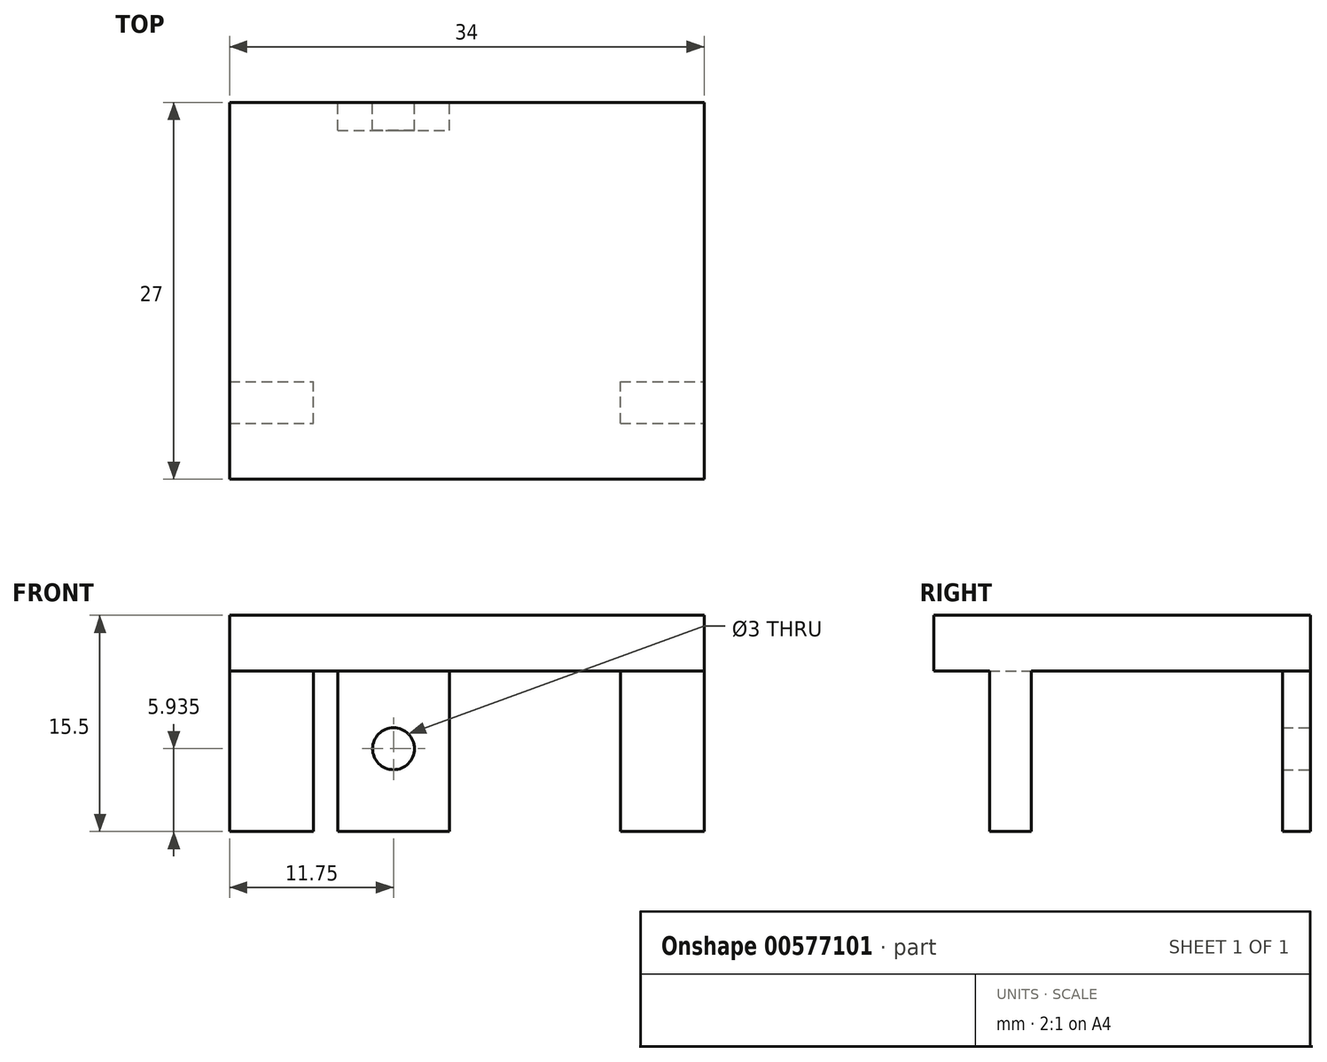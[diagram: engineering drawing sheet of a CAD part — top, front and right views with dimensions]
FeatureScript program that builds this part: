
annotation { "Feature Type Name" : "Feature", "Feature Type Description" : "" }
export const myFeature = defineFeature(function(context is Context, id is Id, definition is map)
    precondition{}
    {
        {
            var Q0;
            Q0=qCreatedBy(makeId("Front.planeOp"),FACE);
            var sketch = newSketch(context, id + "F0", { "sketchPlane" : qUnion([Q0])});
            skLineSegment(sketch, "E0.bottom", {"start": v(0, 0) * mm, "end": v(6, 0) * mm});
            skLineSegment(sketch, "E0.top", {"start": v(0, 15.5) * mm, "end": v(34, 15.5) * mm});
            skLineSegment(sketch, "E0.left", {"start": v(0, 0) * mm, "end": v(0, 15.5) * mm});
            skLineSegment(sketch, "E0.right", {"start": v(34, 0) * mm, "end": v(34, 15.5) * mm});
            skLineSegment(sketch, "E1.top", {"start": v(6, 11.5) * mm, "end": v(28, 11.5) * mm});
            skLineSegment(sketch, "E1.left", {"start": v(6, 0) * mm, "end": v(6, 11.5) * mm});
            skLineSegment(sketch, "E1.right", {"start": v(28, 0) * mm, "end": v(28, 11.5) * mm});
            skLineSegment(sketch, "E2.trimOffspring", {"start": v(28, 0) * mm, "end": v(34, 0) * mm});
            skSolve(sketch);
        }
        {
            var Q0;
            Q0=makeQuery(id+"F0.imprint","IMPRINT",FACE,{"disambiguationData":[TD([[makeQuery(id+"F0.imprint","IMPRINT",EDGE,{"derivedFrom":sQuery(id+"F0.wireOp",EDGE,"E0.bottom")}),1.0]])]});
            extrude(context, id + "F1", {"entities" : qUnion([Q0]), "depth" : 3 * mm, "offsetDistance" : 25 * mm});
        }
        {
            var Q0;
            Q0=makeQuery(id+"F1.opExtrude","CAP_FACE",FACE,{"disambiguationData":[OSD([sQuery(id+"F0.wireOp",EDGE,"E0.bottom"),sQuery(id+"F0.wireOp",EDGE,"E0.top"),sQuery(id+"F0.wireOp",EDGE,"E0.left"),sQuery(id+"F0.wireOp",EDGE,"E0.right"),sQuery(id+"F0.wireOp",EDGE,"E1.top"),sQuery(id+"F0.wireOp",EDGE,"E1.left"),sQuery(id+"F0.wireOp",EDGE,"E1.right"),sQuery(id+"F0.wireOp",EDGE,"E2.trimOffspring")])],"isStart":false});
            var sketch = newSketch(context, id + "F2", { "sketchPlane" : qUnion([Q0])});
            skLineSegment(sketch, "E3.bottom", {"start": v(0, 11.5) * mm, "end": v(34, 11.5) * mm});
            skLineSegment(sketch, "E3.top", {"start": v(0, 15.5) * mm, "end": v(34, 15.5) * mm});
            skLineSegment(sketch, "E3.left", {"start": v(0, 11.5) * mm, "end": v(0, 15.5) * mm});
            skLineSegment(sketch, "E3.right", {"start": v(34, 11.5) * mm, "end": v(34, 15.5) * mm});
            skSolve(sketch);
        }
        {
            var Q0;
            Q0=makeQuery(id+"F2.imprint","IMPRINT",FACE,{"disambiguationData":[TD([[makeQuery(id+"F2.imprint","IMPRINT",EDGE,{"derivedFrom":sQuery(id+"F2.wireOp",EDGE,"E3.top")}),-1.0]])]});
            extrude(context, id + "F3", {"entities" : qUnion([Q0]), "operationType" : NewBodyOperationType.ADD, "depth" : 4 * mm, "offsetDistance" : 25 * mm});
        }
        {
            var Q0;
            Q0 = qSketchRegion(id + "F2", true);
            extrude(context, id + "F4", {"entities" : qUnion([Q0]), "operationType" : NewBodyOperationType.ADD, "oppositeDirection" : true, "depth" : 23 * mm, "offsetDistance" : 25 * mm});
        }
        {
            var Q0;
            Q0=makeQuery(id+"F4.opExtrude","CAP_FACE",FACE,{"disambiguationData":[OSD([sQuery(id+"F2.wireOp",EDGE,"E3.bottom"),sQuery(id+"F2.wireOp",EDGE,"E3.top"),sQuery(id+"F2.wireOp",EDGE,"E3.left"),sQuery(id+"F2.wireOp",EDGE,"E3.right")])],"isStart":false});
            var sketch = newSketch(context, id + "F5", { "sketchPlane" : qUnion([Q0])});
            skLineSegment(sketch, "E4.top", {"start": v(-7.75, 0) * mm, "end": v(-15.75, 0) * mm});
            skLineSegment(sketch, "E4.left", {"start": v(-7.75, 11.5) * mm, "end": v(-7.75, 0) * mm});
            skLineSegment(sketch, "E4.right", {"start": v(-15.75, 11.5) * mm, "end": v(-15.75, 0) * mm});
            skLineSegment(sketch, "E5", {"start": v(-7.75, 11.5) * mm, "end": v(-15.75, 11.5) * mm});
            skSolve(sketch);
        }
        {
            var Q0;
            Q0=makeQuery(id+"F5.imprint","IMPRINT",FACE,{"disambiguationData":[TD([[makeQuery(id+"F5.imprint","IMPRINT",EDGE,{"derivedFrom":sQuery(id+"F5.wireOp",EDGE,"E4.top")}),-1.0]])]});
            extrude(context, id + "F6", {"entities" : qUnion([Q0]), "operationType" : NewBodyOperationType.ADD, "oppositeDirection" : true, "depth" : 2 * mm, "offsetDistance" : 25 * mm});
        }
        {
            var Q0;
            Q0=makeQuery(id+"F6.boolean.opBoolean","MERGE",FACE,{"derivedFrom":[makeQuery(id+"F4.opExtrude","CAP_FACE",FACE,{"disambiguationData":[OSD([sQuery(id+"F2.wireOp",EDGE,"E3.bottom"),sQuery(id+"F2.wireOp",EDGE,"E3.top"),sQuery(id+"F2.wireOp",EDGE,"E3.left"),sQuery(id+"F2.wireOp",EDGE,"E3.right")])],"isStart":false}),makeQuery(id+"F6.opExtrude","CAP_FACE",FACE,{"disambiguationData":[OSD([sQuery(id+"F5.wireOp",EDGE,"E4.top"),sQuery(id+"F5.wireOp",EDGE,"E4.left"),sQuery(id+"F5.wireOp",EDGE,"E4.right"),sQuery(id+"F5.wireOp",EDGE,"E5")])],"isStart":true})]});
            var sketch = newSketch(context, id + "F7", { "sketchPlane" : qUnion([Q0])});
            skArc(sketch, "E6", {"start": v(-10.44, 6.67) * mm, "mid": v(-13.2, 5.56) * mm, "end": v(-10.25, 5.94) * mm});
            skArc(sketch, "E7", {"start": v(-10.25, 5.94) * mm, "mid": v(-10.3, 6.31) * mm, "end": v(-10.44, 6.67) * mm});
            skLineSegment(sketch, "E8.0", {"start": v(0, 0) * mm, "end": v(0, 11.5) * mm, "construction": true});
            skSolve(sketch);
        }
        {
            var Q0;
            Q0=makeQuery(id+"F7.imprint","IMPRINT",FACE,{"disambiguationData":[TD([[makeQuery(id+"F7.imprint","IMPRINT",EDGE,{"derivedFrom":sQuery(id+"F7.wireOp",EDGE,"E6")}),1.0]])]});
            extrude(context, id + "F8", {"entities" : qUnion([Q0]), "operationType" : NewBodyOperationType.REMOVE, "endBound" : BoundingType.UP_TO_NEXT, "oppositeDirection" : true, "depth" : 2 * mm, "offsetDistance" : 25 * mm});
        }
    });
